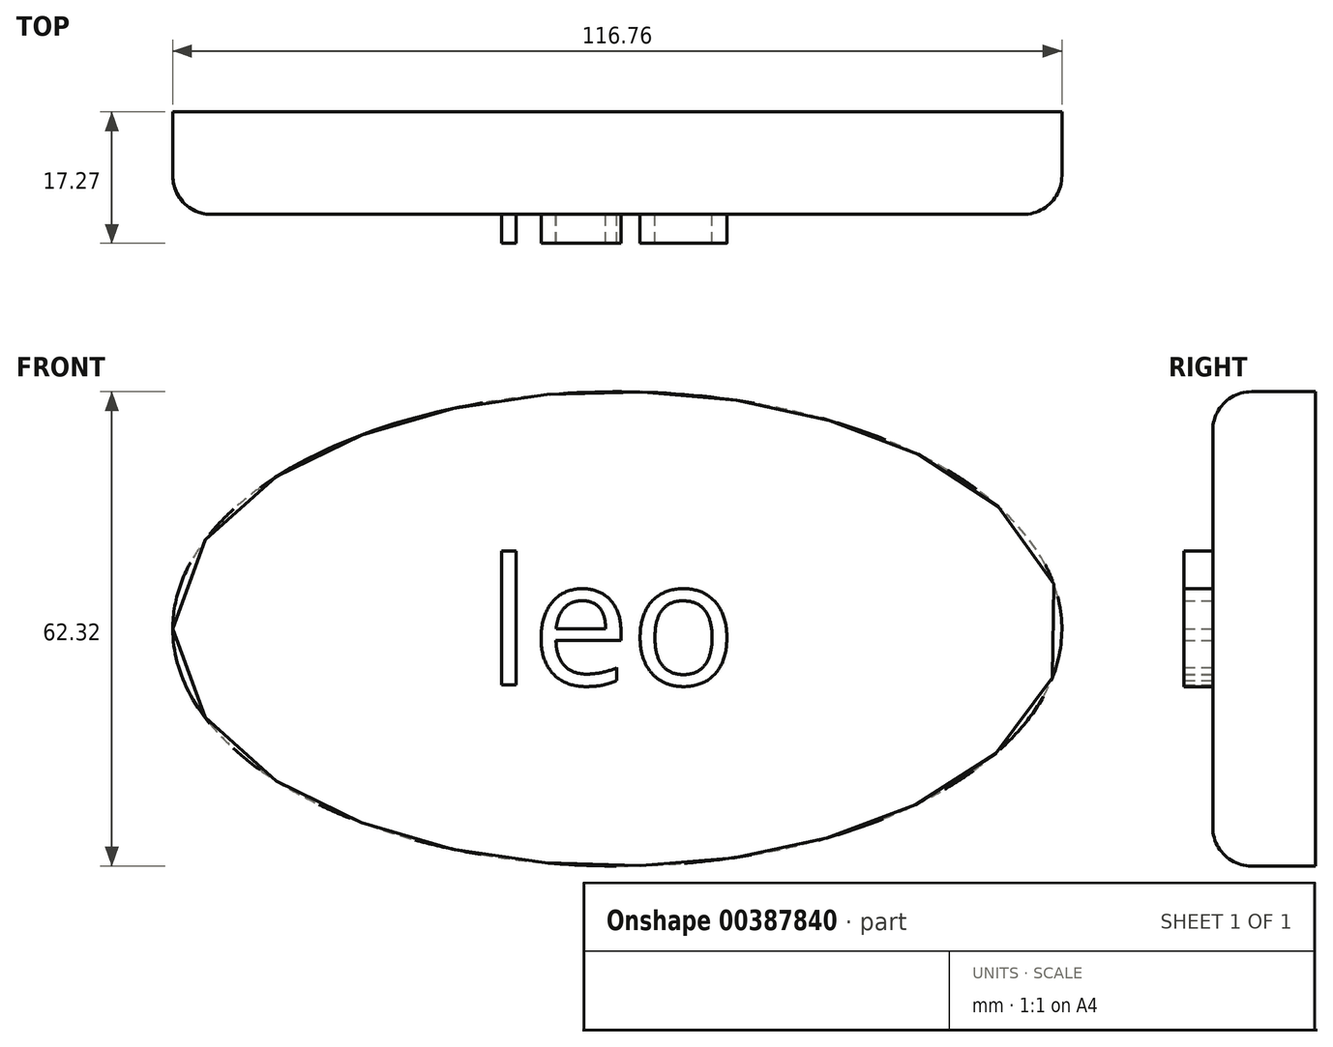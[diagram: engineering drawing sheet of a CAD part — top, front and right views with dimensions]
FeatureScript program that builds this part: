
annotation { "Feature Type Name" : "Feature", "Feature Type Description" : "" }
export const myFeature = defineFeature(function(context is Context, id is Id, definition is map)
    precondition{}
    {
        {
            var Q0;
            Q0=qCreatedBy(makeId("Front.planeOp"),FACE);
            var sketch = newSketch(context, id + "F0", { "sketchPlane" : qUnion([Q0])});
            skEllipse(sketch, "E0", {"center": v(0, 0) * mm, "majorRadius": 58.38 * mm, "minorRadius": 31.16 * mm, "majorAxis": v(-1, 0)});
            skSolve(sketch);
        }
        {
            var Q0;
            Q0=makeQuery(id+"F0.imprint","IMPRINT",FACE,{"disambiguationData":[TD([[makeQuery(id+"F0.imprint","IMPRINT",EDGE,{"derivedFrom":sQuery(id+"F0.wireOp",EDGE,"E0")}),1.0]])]});
            extrude(context, id + "F1", {"entities" : qUnion([Q0]), "depth" : 13.46 * mm});
        }
        {
            var Q0;
            Q0=makeQuery(id+"F1.opExtrude","CAP_EDGE",EDGE,{"disambiguationData":[OSD([sQuery(id+"F0.wireOp",EDGE,"E0")])],"isStart":false});
            fillet(context, id + "F2", {"entities" : qUnion([Q0]), "radius" : 5.08 * mm, "tangentPropagation" : true, "allowEdgeOverflow" : false});
        }
        {
            var Q0;
            Q0=makeQuery(id+"F1.opExtrude","CAP_FACE",FACE,{"disambiguationData":[OSD([sQuery(id+"F0.wireOp",EDGE,"E0")])],"isStart":false});
            var sketch = newSketch(context, id + "F3", { "sketchPlane" : qUnion([Q0])});
            skText(sketch, "E1", { "text": "leo", "fontName": "OpenSans-Regular.ttf"});
            const initialGuessF3  = {"E1": [-0.01718, -0.00736, 1, 0, 0.01669]};
            skSetInitialGuess(sketch, initialGuessF3);
            skSolve(sketch);
        }
        {
            var Q0;
            Q0 = qSketchRegion(id + "F3", true);
            extrude(context, id + "F4", {"entities" : qUnion([Q0]), "operationType" : NewBodyOperationType.ADD, "depth" : 3.8 * mm});
        }
    });
